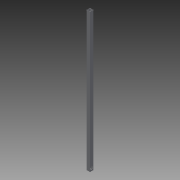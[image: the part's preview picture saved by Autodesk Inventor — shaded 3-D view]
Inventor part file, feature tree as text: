
AUTODESK INVENTOR PART (.ipt)
format: ipt  version: 2015 SP1 (Build 190203100, 203)  size: 83,456 bytes
history: native  units: mm
features: other x3, sketch x3
ambient origin geometry x8: Origin, YZ Plane, XZ Plane, XY Plane, X Axis, Y Axis, Z Axis, Center Point
bodies: Solid1 (feature_tree)
feature tree (6):
  other  "Pied.ipt"
  other  "Solid1::Pied.ipt"
  other  "TaggingFeature1"
  sketch  "Sketch1"  dims[d0=10.0mm]
  sketch  "Sketch2"
  sketch  "Sketch3"
